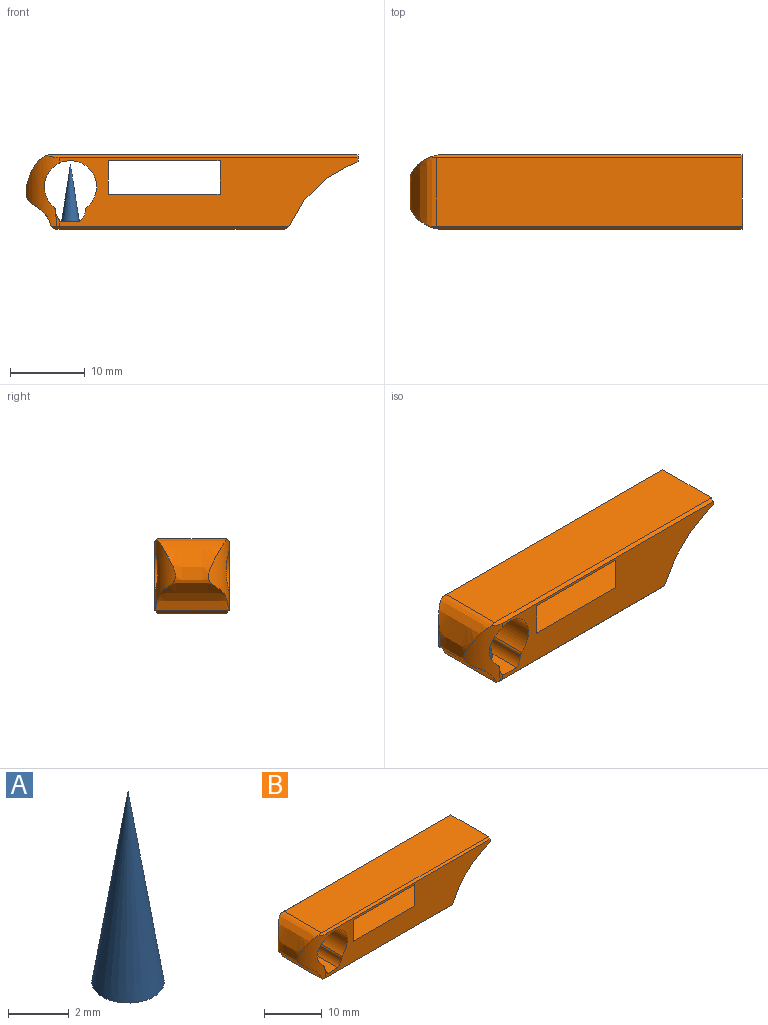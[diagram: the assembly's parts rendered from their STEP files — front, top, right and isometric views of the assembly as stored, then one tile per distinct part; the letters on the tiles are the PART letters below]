
ASSEMBLY  parts=2 mates=1
PART A: 2 faces, bbox 2.4x2.4x7.7 mm
  f0: plane 2.38x2.38mm, normal (0,0,-1), area 4.4mm2, adj f1
  f1: cone r=1.19mm half-angle=8.8deg, axis (0,0,-1), area 29.1mm2, adj f0
PART B: 97 faces, bbox 44.6x10.1x10.1 mm
  f0: extruded ~0.6x0.25mm, area 0.2mm2, adj f1,f9,f20,f72
  f1: extruded ~0.6x0.26mm, area 0.2mm2, adj f0,f2,f20,f72
  f2: extruded ~0.6x0.39mm, area 0.2mm2, adj f1,f3,f20,f72
  f3: plane 1.11x0.6mm, normal (1,0,0), area 0.7mm2, adj f2,f4,f20,f72
  f4: extruded ~0.6x0.41mm, area 0.3mm2, adj f3,f5,f20,f72
  f5: extruded ~0.6x0.26mm, area 0.2mm2, adj f4,f6,f20,f72
  f6: extruded ~0.6x0.25mm, area 0.2mm2, adj f5,f7,f20,f72
  f7: extruded ~0.6x0.41mm, area 0.2mm2, adj f6,f8,f20,f72
  f8: plane 1.11x0.6mm, normal (-1,0,0), area 0.7mm2, adj f7,f9,f20,f72
  f9: extruded ~0.6x0.4mm, area 0.2mm2, adj f0,f8,f20,f72
  f10: extruded ~1.06x0.6mm, area 0.7mm2, adj f11,f19,f20,f63
  f11: extruded ~1.06x0.6mm, area 0.7mm2, adj f10,f12,f20,f63
  f12: extruded ~0.95x0.6mm, area 0.6mm2, adj f11,f13,f20,f63
  f13: plane 1.12x0.6mm, normal (1,0,0), area 0.7mm2, adj f12,f14,f20,f63
  f14: extruded ~0.95x0.6mm, area 0.6mm2, adj f13,f15,f20,f63
  f15: extruded ~1.06x0.6mm, area 0.7mm2, adj f14,f16,f20,f63
  f16: extruded ~1.06x0.6mm, area 0.7mm2, adj f15,f17,f20,f63
  f17: extruded ~0.94x0.6mm, area 0.6mm2, adj f16,f18,f20,f63
  f18: plane 1.12x0.6mm, normal (-1,0,0), area 0.7mm2, adj f17,f19,f20,f63
  f19: extruded ~0.94x0.6mm, area 0.6mm2, adj f10,f18,f20,f63
  f20: plane 3.7x2.85mm, normal (0,1,0), area 7.9mm2, adj f0,f1,f2,f3,f4,f5,f6,f7
  f21: extruded ~0.6x0.25mm, area 0.2mm2, adj f22,f30,f41,f65
  f22: extruded ~0.6x0.26mm, area 0.2mm2, adj f21,f23,f41,f65
  f23: extruded ~0.6x0.39mm, area 0.2mm2, adj f22,f24,f41,f65
  f24: plane 1.11x0.6mm, normal (1,0,0), area 0.7mm2, adj f23,f25,f41,f65
  f25: extruded ~0.6x0.41mm, area 0.3mm2, adj f24,f26,f41,f65
  f26: extruded ~0.6x0.26mm, area 0.2mm2, adj f25,f27,f41,f65
  f27: extruded ~0.6x0.25mm, area 0.2mm2, adj f26,f28,f41,f65
  f28: extruded ~0.6x0.41mm, area 0.2mm2, adj f27,f29,f41,f65
  f29: plane 1.11x0.6mm, normal (-1,0,0), area 0.7mm2, adj f28,f30,f41,f65
  f30: extruded ~0.6x0.4mm, area 0.2mm2, adj f21,f29,f41,f65
  f31: extruded ~1.06x0.6mm, area 0.7mm2, adj f32,f40,f41,f63
  f32: extruded ~1.06x0.6mm, area 0.7mm2, adj f31,f33,f41,f63
  f33: extruded ~0.95x0.6mm, area 0.6mm2, adj f32,f34,f41,f63
  f34: plane 1.12x0.6mm, normal (1,0,0), area 0.7mm2, adj f33,f35,f41,f63
  f35: extruded ~0.95x0.6mm, area 0.6mm2, adj f34,f36,f41,f63
  f36: extruded ~1.06x0.6mm, area 0.7mm2, adj f35,f37,f41,f63
  f37: extruded ~1.06x0.6mm, area 0.7mm2, adj f36,f38,f41,f63
  f38: extruded ~0.94x0.6mm, area 0.6mm2, adj f37,f39,f41,f63
  f39: plane 1.12x0.6mm, normal (-1,0,0), area 0.7mm2, adj f38,f40,f41,f63
  f40: extruded ~0.94x0.6mm, area 0.6mm2, adj f31,f39,f41,f63
  f41: plane 3.7x2.85mm, normal (0,1,0), area 7.9mm2, adj f21,f22,f23,f24,f25,f26,f27,f28
  f42: extruded ~0.6x0.25mm, area 0.2mm2, adj f43,f51,f62,f64
  f43: extruded ~0.6x0.26mm, area 0.2mm2, adj f42,f44,f62,f64
  f44: extruded ~0.6x0.39mm, area 0.2mm2, adj f43,f45,f62,f64
  f45: plane 1.11x0.6mm, normal (1,0,0), area 0.7mm2, adj f44,f46,f62,f64
  f46: extruded ~0.6x0.41mm, area 0.3mm2, adj f45,f47,f62,f64
  f47: extruded ~0.6x0.26mm, area 0.2mm2, adj f46,f48,f62,f64
  f48: extruded ~0.6x0.25mm, area 0.2mm2, adj f47,f49,f62,f64
  f49: extruded ~0.6x0.41mm, area 0.2mm2, adj f48,f50,f62,f64
  f50: plane 1.11x0.6mm, normal (-1,0,0), area 0.7mm2, adj f49,f51,f62,f64
  f51: extruded ~0.6x0.4mm, area 0.2mm2, adj f42,f50,f62,f64
  f52: extruded ~1.06x0.6mm, area 0.7mm2, adj f53,f61,f62,f63
  f53: extruded ~1.06x0.6mm, area 0.7mm2, adj f52,f54,f62,f63
  f54: extruded ~0.95x0.6mm, area 0.6mm2, adj f53,f55,f62,f63
  f55: plane 1.12x0.6mm, normal (1,0,0), area 0.7mm2, adj f54,f56,f62,f63
  f56: extruded ~0.95x0.6mm, area 0.6mm2, adj f55,f57,f62,f63
  f57: extruded ~1.06x0.6mm, area 0.7mm2, adj f56,f58,f62,f63
  f58: extruded ~1.06x0.6mm, area 0.7mm2, adj f57,f59,f62,f63
  f59: extruded ~0.94x0.6mm, area 0.6mm2, adj f58,f60,f62,f63
  f60: plane 1.12x0.6mm, normal (-1,0,0), area 0.7mm2, adj f59,f61,f62,f63
  f61: extruded ~0.94x0.6mm, area 0.6mm2, adj f52,f60,f62,f63
  f62: plane 3.7x2.85mm, normal (0,1,0), area 7.9mm2, adj f42,f43,f44,f45,f46,f47,f48,f49
  f63: plane 40.03x9.2mm, normal (0,1,0), area 132.5mm2, adj f10,f11,f12,f13,f14,f15,f16,f17
  f64: plane 2.14x0.66mm, normal (0,1,0), area 1.3mm2, adj f42,f43,f44,f45,f46,f47,f48,f49
  f65: plane 2.14x0.66mm, normal (0,1,0), area 1.3mm2, adj f21,f22,f23,f24,f25,f26,f27,f28
  f66: plane 30.77x0.4mm, normal (0,0.71,-0.71), area 17.2mm2, adj f63,f67,f71,f75,f95
  f67: plane 9.89x0.6mm, normal (0.5,0,-0.87), area 6.6mm2, adj f66,f68,f75,f95
  f68: plane 30.77x0.4mm, normal (0,-0.71,-0.71), area 17.2mm2, adj f67,f69,f75,f95,f96
  f69: cone r=4.8mm half-angle=45deg, axis (0,0,1), area 0.5mm2, adj f68,f70,f74,f75,f80
  f70: plane 9.74x0.52mm, normal (-0.61,0,-0.8), area 6mm2, adj f69,f71,f74,f75
  f71: cone r=4.8mm half-angle=45deg, axis (0,0,1), area 0.5mm2, adj f66,f70,f73,f74,f75
  f72: plane 2.14x0.66mm, normal (0,1,0), area 1.3mm2, adj f0,f1,f2,f3,f4,f5,f6,f7
  f73: cylinder r=5mm len=9.5mm, axis (0,0,1), area 25.5mm2, adj f63,f71,f74,f76,f81,f82,f88
  f74: extruded ~9.75x9.61mm, area 92.3mm2, adj f69,f70,f71,f73,f76,f78,f79,f80
  f75: plane 30.7x9.2mm, normal (0,0,-1), area 282.4mm2, adj f66,f67,f68,f69,f70,f71
  f76: plane 41.83x0.54mm, normal (0,0.71,0.71), area 23.3mm2, adj f63,f73,f74,f77,f78
  f77: plane 10x0.93mm, normal (1,0,0), area 9.1mm2, adj f63,f76,f78,f79,f92,f96
  f78: plane 40.99x9.2mm, normal (0,0,1), area 377.1mm2, adj f74,f76,f77,f79
  f79: plane 41.83x0.54mm, normal (0,-0.71,0.71), area 23.3mm2, adj f74,f77,f78,f80,f96
  f80: cylinder r=5mm len=9.5mm, axis (0,0,1), area 25.2mm2, adj f69,f74,f79,f81,f82,f88,f96
  f81: cylinder r=3.5mm len=10mm, axis (0,-1,0), area 172.3mm2, adj f63,f73,f80,f82,f91,f96
  f82: cylinder r=0.5mm len=9.94mm, axis (0,-1,0), area 4.4mm2, adj f73,f80,f81,f88
  f83: plane 15x10mm, normal (-0.55,0.83,0), area 67.6mm2, adj f84,f85,f86,f96
  f84: plane 25x10mm, normal (0,0,1), area 216.7mm2, adj f63,f83,f86,f87,f96
  f85: plane 30x10mm, normal (0,0,-1), area 225mm2, adj f63,f83,f87,f96
  f86: plane 5x4.5mm, normal (-0.67,0,0.74), area 11.2mm2, adj f63,f83,f84
  f87: plane 10x4.5mm, normal (1,0,0), area 45mm2, adj f63,f84,f85,f96
  f88: cylinder r=2mm len=10mm, axis (0,-1,0), area 18.5mm2, adj f63,f73,f80,f82,f89,f96
  f89: plane 10x2.38mm, normal (0,0,1), area 23.8mm2, adj f63,f88,f90,f96
  f90: cylinder r=2mm len=10mm, axis (0,-1,0), area 18.5mm2, adj f63,f89,f91,f96
  f91: cylinder r=0.5mm len=10mm, axis (0,-1,0), area 4.4mm2, adj f63,f81,f90,f96
  f92: plane 10x1.81mm, normal (0.42,0,-0.91), area 20mm2, adj f63,f77,f93,f96
  f93: plane 10x2.6mm, normal (0.5,0,-0.87), area 30mm2, adj f63,f92,f94,f96
  f94: plane 10x2.83mm, normal (0.71,0,-0.71), area 40mm2, adj f63,f93,f95,f96
  f95: plane 10x3.55mm, normal (0.87,0,-0.5), area 41mm2, adj f63,f66,f67,f68,f94,f96
  f96: plane 40.03x9.2mm, normal (0,-1,0), area 216.2mm2, adj f68,f77,f79,f80,f81,f83,f84,f85
PLACE A t=(14.52,3.69,-1.76)mm
PLACE B t=(14.52,3.69,-1.76)mm
MATE fastened A.f1 <-> B.f89  axis (0,0,-1) through (-14.52,-1.31,-0.76)mm
